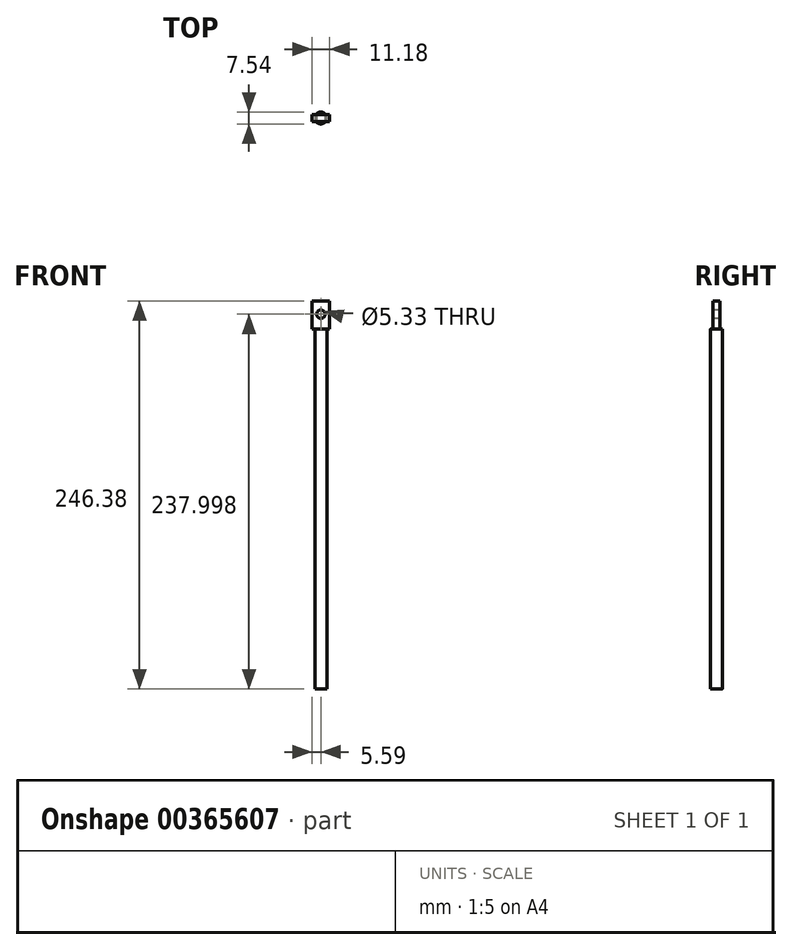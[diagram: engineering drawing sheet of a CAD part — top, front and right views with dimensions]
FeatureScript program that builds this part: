
annotation { "Feature Type Name" : "Feature", "Feature Type Description" : "" }
export const myFeature = defineFeature(function(context is Context, id is Id, definition is map)
    precondition{}
    {
        {
            var Q0;
            Q0=qCreatedBy(makeId("Top.planeOp"),FACE);
            var sketch = newSketch(context, id + "F0", { "sketchPlane" : qUnion([Q0])});
            skCircle(sketch, "E0", {"center": v(0, 0) * mm, "radius": 3.77 * mm});
            skSolve(sketch);
        }
        {
            var Q0;
            Q0 = qSketchRegion(id + "F0", true);
            extrude(context, id + "F1", {"entities" : qUnion([Q0]), "depth" : 228.6 * mm, "offsetDistance" : 25.4 * mm});
        }
        {
            var Q0;
            Q0=makeQuery(id+"F1.opExtrude","CAP_FACE",FACE,{"disambiguationData":[OSD([sQuery(id+"F0.wireOp",EDGE,"E0")])],"isStart":false});
            var sketch = newSketch(context, id + "F2", { "sketchPlane" : qUnion([Q0])});
            skLineSegment(sketch, "E1.bottom", {"start": v(5.59, -2.17) * mm, "end": v(-5.59, -2.17) * mm});
            skLineSegment(sketch, "E1.top", {"start": v(5.59, 2.17) * mm, "end": v(-5.59, 2.17) * mm});
            skLineSegment(sketch, "E1.left", {"start": v(5.59, -2.17) * mm, "end": v(5.59, 2.17) * mm});
            skLineSegment(sketch, "E1.right", {"start": v(-5.59, -2.17) * mm, "end": v(-5.59, 2.17) * mm});
            skPoint(sketch, "E1.middle", {"position": v(0, 0) * mm});
            skSolve(sketch);
        }
        {
            var Q0;
            Q0 = qSketchRegion(id + "F2", true);
            extrude(context, id + "F3", {"entities" : qUnion([Q0]), "operationType" : NewBodyOperationType.ADD, "depth" : 17.78 * mm, "offsetDistance" : 25.4 * mm});
        }
        {
            var Q0;
            Q0=makeQuery(id+"F3.opExtrude","SWEPT_FACE",FACE,{"disambiguationData":[OSD([sQuery(id+"F2.wireOp",EDGE,"E1.top")])]});
            var sketch = newSketch(context, id + "F4", { "sketchPlane" : qUnion([Q0])});
            skPoint(sketch, "E2", {"position": v(0, 238) * mm});
            skSolve(sketch);
        }
        {
            var Q0;
            Q0=sQuery(id+"F4.wireOp",VERTEX,"E2");
            var Q1;
            Q1=makeQuery(id+"F1.opExtrude","SWEPT_BODY",BODY,{"disambiguationData":[OSD([sQuery(id+"F0.wireOp",EDGE,"E0")])]});
            hole(context, id + "F5", {"style" : HoleStyle.SIMPLE, "endStyle" : HoleEndStyle.THROUGH, "holeDiameter" : 5.33 * mm, "majorDiameter" : 6.35 * mm, "isTappedThrough" : true, "tappedDepth" : 12.7 * mm, "tapClearance" : 3, "locations" : qUnion([Q0]), "scope" : qUnion([Q1]), "startStyle" : HoleStartStyle.SKETCH});
        }
    });
